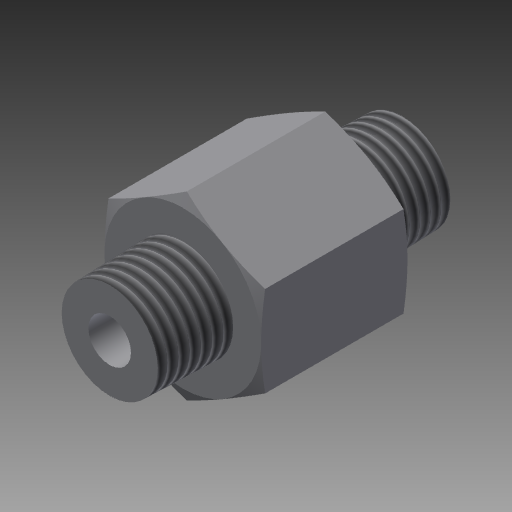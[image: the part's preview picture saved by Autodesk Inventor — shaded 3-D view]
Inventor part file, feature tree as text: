
AUTODESK INVENTOR PART (.ipt)
format: ipt  version: 2017.1 (Build 211199000, 199)  size: 178,688 bytes
history: native  units: in
note: dims shown in document units (in); Inventor stores cm internally (conversion verified against a paired STEP export)
features: sketch x4, extrude x3, plane x2, thread x2, other x1, hole x1, revolve x1, mirror x1, reference x1
ambient origin geometry x8: Origin, YZ Plane, XZ Plane, XY Plane, X Axis, Y Axis, Z Axis, Center Point
bodies: Solid1 (feature_tree)
feature tree (16):
  sketch  "Sketch1"  dims[d2=0.5in d3=0.0in d20=0.25in d21=-0.0123in]
  extrude  "Extrusion1"  Depth=0.25in
  plane  "Work Plane1"
  other  "Work Axis3"
  extrude  "Extrusion3"  Depth=0.25in
  thread  "Thread2"  [1 undecoded]
  hole  "Hole2"  [1 undecoded]
  extrude  "Extrusion4"  Depth=0.0414in
  thread  "Thread3"  [1 undecoded]
  revolve  "Revolution3"  [1 undecoded]
  plane  "Work Plane4"
  mirror  "Mirror4"
  sketch  "Sketch6"  dims[d22=0.392in d23=0.0in]
  reference  "Reference3"
  sketch  "Sketch7"  dims[d24=0.13in d25=0.75in d26=0.375in d27=0.25in d28=0.5635in d29=1.0in d30=0.8108in d31=0.25in d32=-0.0123in d33=0.392in d34=0.0in]
  sketch  "Sketch8"  dims[d35=90.0deg d36=0.5355in d37=0.0414in d38=0.0415in]
note: 4 required parameter values undecoded (feature->parameter linkage not recoverable at this tier; creation-order binding heuristic only, values carry confidence <= 0.55)
